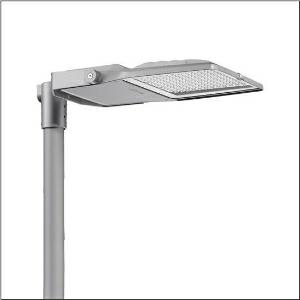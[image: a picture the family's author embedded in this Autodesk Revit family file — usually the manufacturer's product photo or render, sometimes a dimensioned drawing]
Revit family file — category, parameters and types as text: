
# Revit family: floodlight_fl_21_iq_midi___pl33t_5xa7782f2f3a_348f
name_source: partatom
category: Lighting Fixtures
units: mm (PartAtom-declared; Revit-internal decimal feet)

## family parameters
Cut with Voids When Loaded = No
Host = Face
Light Source = No
Part Type = Normal
Room Calculation Point = No
Round Connector Dimension = Use Diameter
Shared = No

## types (1)
- --- (1 x LED, 35350 lm, 270.2 W, 3000K)
    Apparent Load = 270 VA
    CIE Flux Codes = 26 75 99 100 100
    Color Rendering = 70
    Color Temperature = 3000K
    Default Elevation = 1800 mm
    Description = Floodlight FL 21 iQ midi, floodlight, primary light control with lens, of PMMA, primary optical cover: protective disc, of toughened safety glass, transparent, light distribution: PL33T, light emission: direct distribution, installation type: surface-mounted, LED, High Power LED, rated luminous flux: 35.350lm, luminous efficacy: 131lm/W, light colour: 730, colour temperature: 3000K, control gear: iQ Street-Remote/DALI, control: optimised constant luminous flux control (CLO 2.0), Desk-Remote (wireless, voltage-free reading and setting of iQ features in the workshop via application-optimized NFC function/RFID function), Smart-Wire, Night-Set, Temp-Guard, Auto-Match, Street-Remote, with terminal, 6-pole, mains connection: 220..240V, AC, 50/60Hz, start of lifetime: 270W, end of service life: 287W, reduction: 117W, luminaire housing, of diecast aluminium, powder-coated, Siteco® metallic grey (DB 702S), corrosivity category C5 mid according to DIN EN ISO 12944, suitable for swimming pools, chlorine-resistant, sealing non-destructively replaceable, please order mast flange separately, mast bracket, of steel, galvanised, powder-coated, Siteco® metallic grey (DB 702S), protection rating (complete): IP66, insulation class (complete): insulation class II (safety insulation), certification: CE, ENEC, VDE, protection symbol: D, impact resistance: IK08, permissible operating ambient temperature: -40..+40°C, permissible operating ambient temperature for outdoor applications: -40..+50°C, standard: DIN EN 12944, LABS conformity tested according to VDMA 24364:2018-05, packaging unit: 1 piece

Light Distribution: PL33T
    Height = 76 mm
    Lamp = 1 x LED
    Lamp Light Flux = 35350 lm
    Lamp Power = 270.2 W
    Lamp count = 1
    Length = 657 mm
    Luminous efficacy = 131 lm/W
    Manufacturer = Siteco
    ModVariant = No
    Model = 5XA7782F2F3A
    Number of Poles = 1
    OnlyDefault = Yes
    Power Factor = 1
    Product Name = Floodlight FL 21 iQ midi | PL33T
    Product group = floodlight | pylon annexe
    ProductGroupID = 6200
    Protection Class = Protection class II
    Protection Degree = IP 66
    RLX_Detail_Level = 1
    RLX_Emergency_Light_Flux = 0 lm
    RLX_Emergency_Type = 0
    RLX_Emergency_Type_DB = No
    RlxData = <blob elided: 153513 chars, md5=2c41e2d8>
    Socket = socket
    Standby Power = 0 W
    System Light Flux = 35350 lm
    System Power = 270 W
    Type Comments = factory setting: luminous flux: 100 % | dim-lin: 254 | 620 mA
    Type Image = l_1007123.jpg
    URL = http://relux.com
    VarID = @adj_103374
    Voltage = 0 V
    Weight = 0.00 kg
    Width = 442 mm

## geometry (parser evidence)
native form markers: Blend x4, Sweep x11
no freeform markers — native parametric forms only
